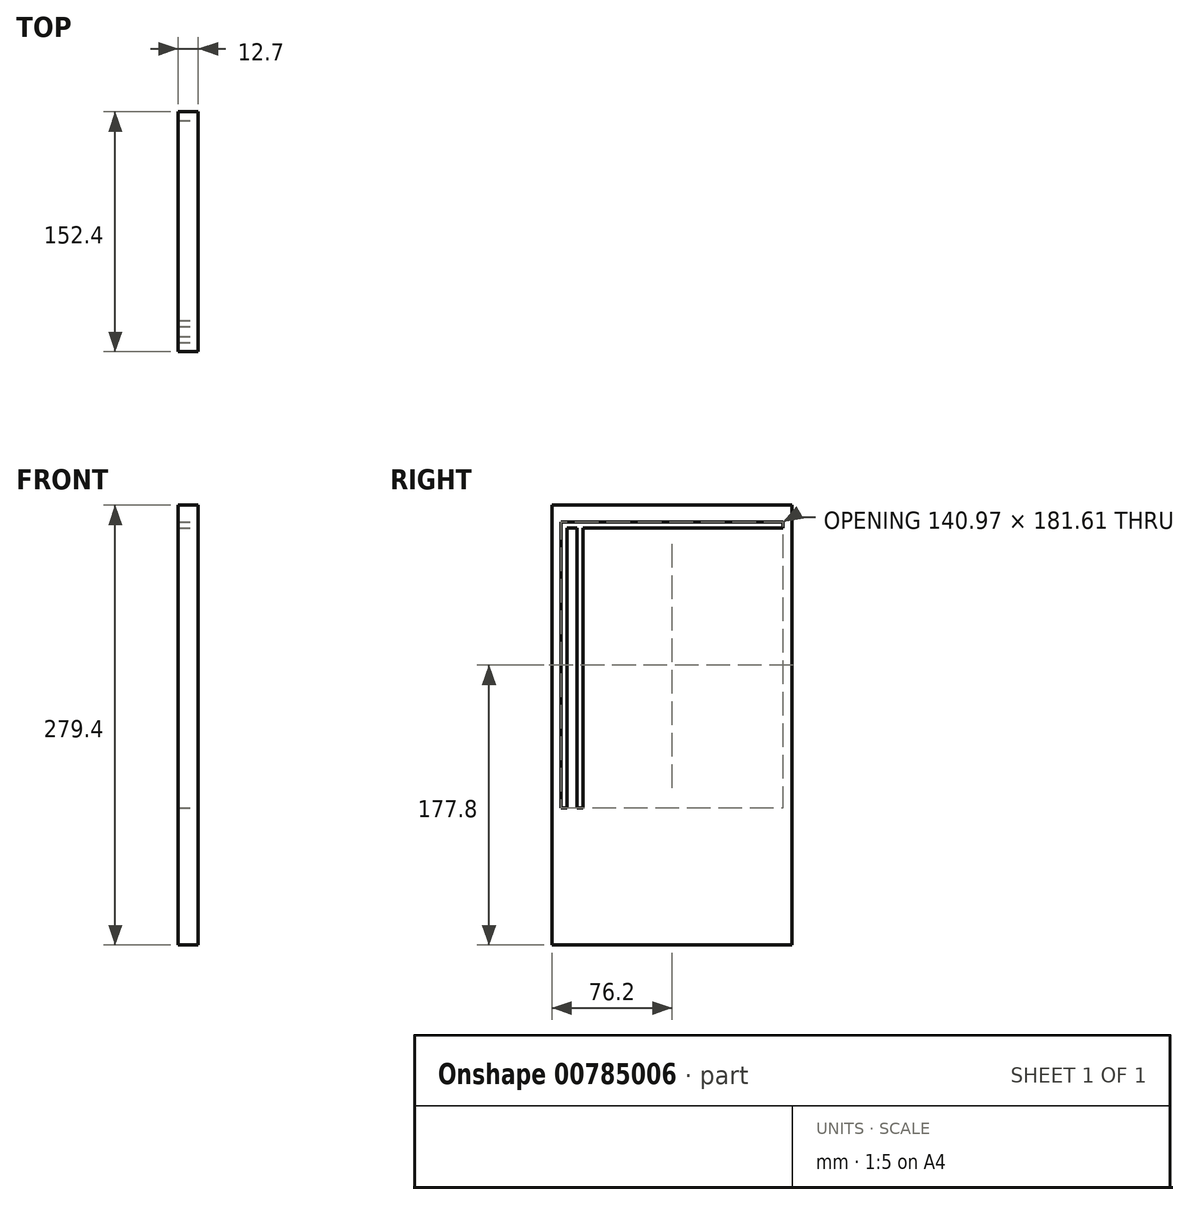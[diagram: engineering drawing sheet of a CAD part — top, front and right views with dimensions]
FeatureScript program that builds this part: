
annotation { "Feature Type Name" : "Feature", "Feature Type Description" : "" }
export const myFeature = defineFeature(function(context is Context, id is Id, definition is map)
    precondition{}
    {
        {
            var Q0;
            Q0=qCreatedBy(makeId("Right.planeOp"),FACE);
            var sketch = newSketch(context, id + "F0", { "sketchPlane" : qUnion([Q0])});
            skLineSegment(sketch, "E0.bottom", {"start": v(76.2, 139.7) * mm, "end": v(-76.2, 139.7) * mm});
            skLineSegment(sketch, "E0.top", {"start": v(76.2, -139.7) * mm, "end": v(-76.2, -139.7) * mm});
            skLineSegment(sketch, "E0.left", {"start": v(76.2, 139.7) * mm, "end": v(76.2, -139.7) * mm});
            skLineSegment(sketch, "E0.right", {"start": v(-76.2, 139.7) * mm, "end": v(-76.2, -139.7) * mm});
            skPoint(sketch, "E0.middle", {"position": v(0, 0) * mm});
            skLineSegment(sketch, "E1.bottom", {"start": v(-70.48, -52.7) * mm, "end": v(-66.67, -52.7) * mm});
            skLineSegment(sketch, "E1.top", {"start": v(-70.49, 128.9) * mm, "end": v(-66.68, 128.9) * mm});
            skLineSegment(sketch, "E1.left", {"start": v(-70.49, -52.7) * mm, "end": v(-70.49, 128.9) * mm});
            skLineSegment(sketch, "E1.right", {"start": v(-66.68, -52.7) * mm, "end": v(-66.68, 128.9) * mm});
            skLineSegment(sketch, "E2.top", {"start": v(-60.33, 128.9) * mm, "end": v(-56.52, 128.9) * mm});
            skLineSegment(sketch, "E2.left", {"start": v(-60.33, 112.4) * mm, "end": v(-60.33, 128.9) * mm});
            skLineSegment(sketch, "E2.right", {"start": v(-56.52, 112.4) * mm, "end": v(-56.52, 128.9) * mm});
            skLineSegment(sketch, "E3.bottom", {"start": v(-70.49, 128.9) * mm, "end": v(70.48, 128.9) * mm});
            skLineSegment(sketch, "E3.top", {"start": v(-70.49, 125.1) * mm, "end": v(70.48, 125.1) * mm});
            skLineSegment(sketch, "E3.left", {"start": v(-70.49, 128.9) * mm, "end": v(-70.49, 125.1) * mm});
            skLineSegment(sketch, "E3.right", {"start": v(70.48, 128.9) * mm, "end": v(70.48, 125.1) * mm});
            skLineSegment(sketch, "E4.bottom", {"start": v(-60.32, -52.7) * mm, "end": v(-56.52, -52.7) * mm});
            skLineSegment(sketch, "E4.left", {"start": v(-60.32, -52.7) * mm, "end": v(-60.32, -40) * mm});
            skLineSegment(sketch, "E4.right", {"start": v(-56.52, -52.7) * mm, "end": v(-56.52, 112.4) * mm});
            skLineSegment(sketch, "E5", {"start": v(-60.32, 112.4) * mm, "end": v(-60.32, -40) * mm});
            skSolve(sketch);
        }
        {
            var Q0;
            Q0=makeQuery(id+"F0.imprint","IMPRINT",FACE,{"disambiguationData":[TD([[makeQuery(id+"F0.imprint","IMPRINT",EDGE,{"derivedFrom":sQuery(id+"F0.wireOp",EDGE,"E0.bottom")}),1.0]])]});
            extrude(context, id + "F1", {"entities" : qUnion([Q0]), "oppositeDirection" : true, "depth" : 12.7 * mm, "offsetDistance" : 25.4 * mm});
        }
    });
